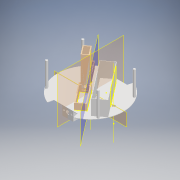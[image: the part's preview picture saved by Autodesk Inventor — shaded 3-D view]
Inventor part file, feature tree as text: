
AUTODESK INVENTOR PART (.ipt)
format: ipt  version: 2020 (Build 240168000, 168)  size: 551,424 bytes
history: native  units: mm
features: sketch x13, other x10, extrude x6, reference x5, plane x3, projected_geometry x3, mirror x2, revolve x1, pattern_circular x1
ambient origin geometry x8: Origin, YZ Plane, XZ Plane, XY Plane, X Axis, Y Axis, Z Axis, Center Point
bodies: Solid1 (feature_tree)
feature tree (44):
  other  "Assembly1.iam"
  other  "KonstrukcijaDonjiDio_v.1.1.ipt:1"
  other  "DropMechanism_v.1.2.ipt:1"
  extrude  "Extrusion1"  Depth=5.0mm
  mirror  "Mirror1"
  plane  "Work Plane3"
  mirror  "Mirror2"
  sketch  "Sketch6"  dims[d43=11.0mm d44=13.0mm]
  sketch  "Sketch7"  dims[d45=4.0mm d46=0.0mm d47=0.5mm]
  extrude  "Extrusion2"  Depth=2.0mm TaperAngle=0.0deg
  extrude  "Extrusion3"  Depth=8.0mm
  extrude  "Extrusion5"  Depth=5.0mm
  sketch  "Sketch11"  dims[d22=0.5mm]
  sketch  "Sketch12"  dims[d23=0.872665mm]
  other  "Work Axis2"
  extrude  "Extrusion9"  Depth=13.0mm
  sketch  "Sketch18"  dims[d25=0.872665mm]
  other  "Work Axis3"
  revolve  "Revolution1"  [1 undecoded]
  pattern_circular  "Circular Pattern4"  Count=20 Angle=360.0deg
  extrude  "Extrusion10"  Depth=1.0mm TaperAngle=0.0deg
  plane  "Work Plane1"
  sketch  "Sketch2"  dims[d0=10.0mm d1=5.0mm]
  plane  "Work Plane1_1"
  sketch  "Sketch3"  dims[d2=55.0mm d3=0.0mm d4=2.0mm d5=0.0mm]
  sketch  "Sketch4"  dims[d6=2.0mm d7=0.0mm d11=8.0mm]
  other  "Srf1"
  sketch  "Sketch5"  dims[d12=1.0mm d13=0.0mm d42=5.0mm]
  projected_geometry  "Projected Loop1"
  projected_geometry  "Projected Loop2"
  sketch  "Sketch8"  dims[d48=2.164208mm d49=200.0mm d50=360.0deg]
  projected_geometry  "Projected Loop3"
  sketch  "Sketch10"  dims[d52=6.0mm d53=1.0mm d54=0.0mm]
  reference  "Reference1"
  reference  "Reference2"
  reference  "Reference3"
  reference  "Reference4"
  reference  "Reference5"
  sketch  "Sketch17"  dims[d24=0.5mm]
  sketch  "Sketch19"
  other  "Srf1::Derived"
  other  "<userpath>\Documents\Draws_Inventor\Inventor_Robocup\Robot_assembly.iam"
  other  "Robot_assembly.iam"
  other  "Extension board:1"
note: 1 required parameter value undecoded (feature->parameter linkage not recoverable at this tier; creation-order binding heuristic only, values carry confidence <= 0.55)
